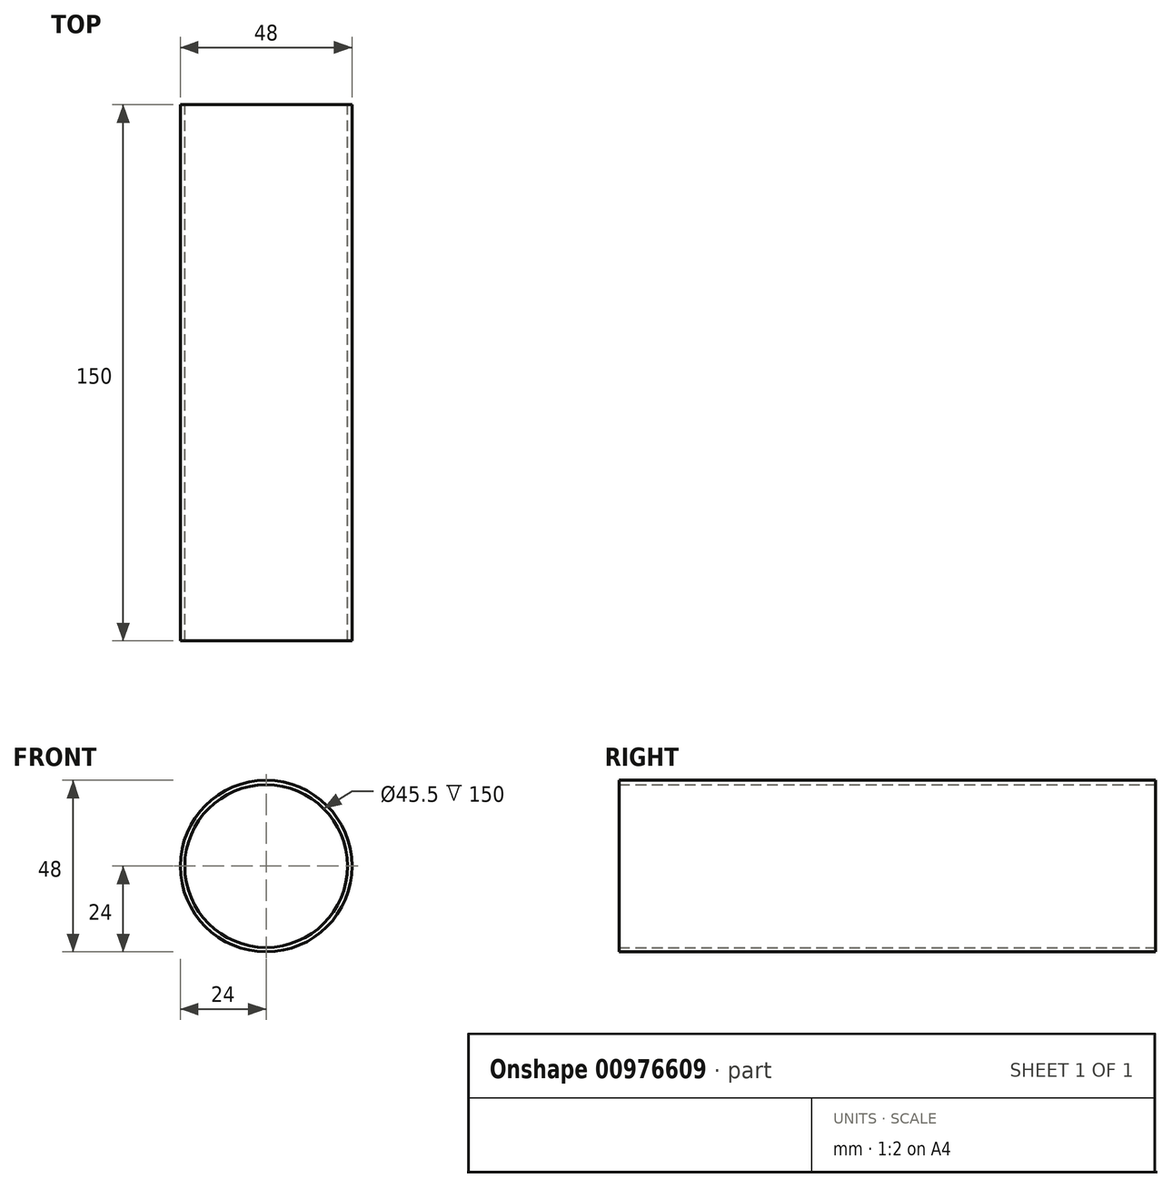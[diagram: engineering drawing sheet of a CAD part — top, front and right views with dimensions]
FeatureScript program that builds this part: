
annotation { "Feature Type Name" : "Feature", "Feature Type Description" : "" }
export const myFeature = defineFeature(function(context is Context, id is Id, definition is map)
    precondition{}
    {
        {
            var Q0;
            Q0=qCreatedBy(makeId("Front.planeOp"),FACE);
            var sketch = newSketch(context, id + "F0", { "sketchPlane" : qUnion([Q0])});
            skCircle(sketch, "E0", {"center": v(0, 0) * mm, "radius": 24 * mm});
            skCircle(sketch, "E1", {"center": v(0, 0) * mm, "radius": 22.75 * mm});
            skSolve(sketch);
        }
        {
            var Q0;
            Q0=makeQuery(id+"F0.imprint","IMPRINT",FACE,{"disambiguationData":[TD([[makeQuery(id+"F0.imprint","IMPRINT",EDGE,{"derivedFrom":sQuery(id+"F0.wireOp",EDGE,"E0")}),1.0]])]});
            extrude(context, id + "F1", {"entities" : qUnion([Q0]), "depth" : 150 * mm, "offsetDistance" : 25 * mm});
        }
    });
